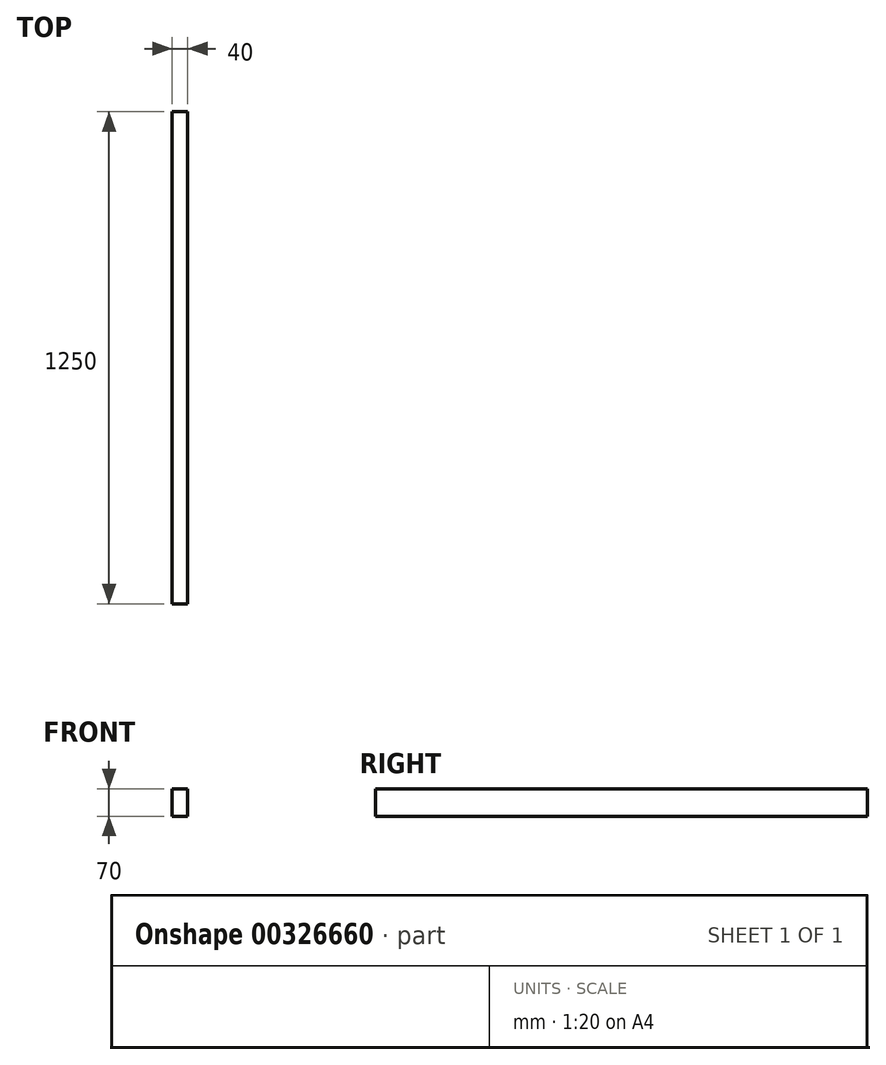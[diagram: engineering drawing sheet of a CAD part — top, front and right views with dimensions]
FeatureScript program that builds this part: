
annotation { "Feature Type Name" : "Feature", "Feature Type Description" : "" }
export const myFeature = defineFeature(function(context is Context, id is Id, definition is map)
    precondition{}
    {
        {
            var Q0;
            Q0=qCreatedBy(makeId("Front.planeOp"),FACE);
            var sketch = newSketch(context, id + "F0", { "sketchPlane" : qUnion([Q0])});
            skLineSegment(sketch, "E0.bottom", {"start": v(0, 0) * mm, "end": v(40, 0) * mm});
            skLineSegment(sketch, "E0.top", {"start": v(0, 70) * mm, "end": v(40, 70) * mm});
            skLineSegment(sketch, "E0.left", {"start": v(0, 0) * mm, "end": v(0, 70) * mm});
            skLineSegment(sketch, "E0.right", {"start": v(40, 0) * mm, "end": v(40, 70) * mm});
            skSolve(sketch);
        }
        {
            var Q0;
            Q0=makeQuery(id+"F0.imprint","IMPRINT",FACE,{"disambiguationData":[TD([[makeQuery(id+"F0.imprint","IMPRINT",EDGE,{"derivedFrom":sQuery(id+"F0.wireOp",EDGE,"E0.bottom")}),1.0]])]});
            extrude(context, id + "F1", {"entities" : qUnion([Q0]), "depth" : 1250 * mm});
        }
    });
